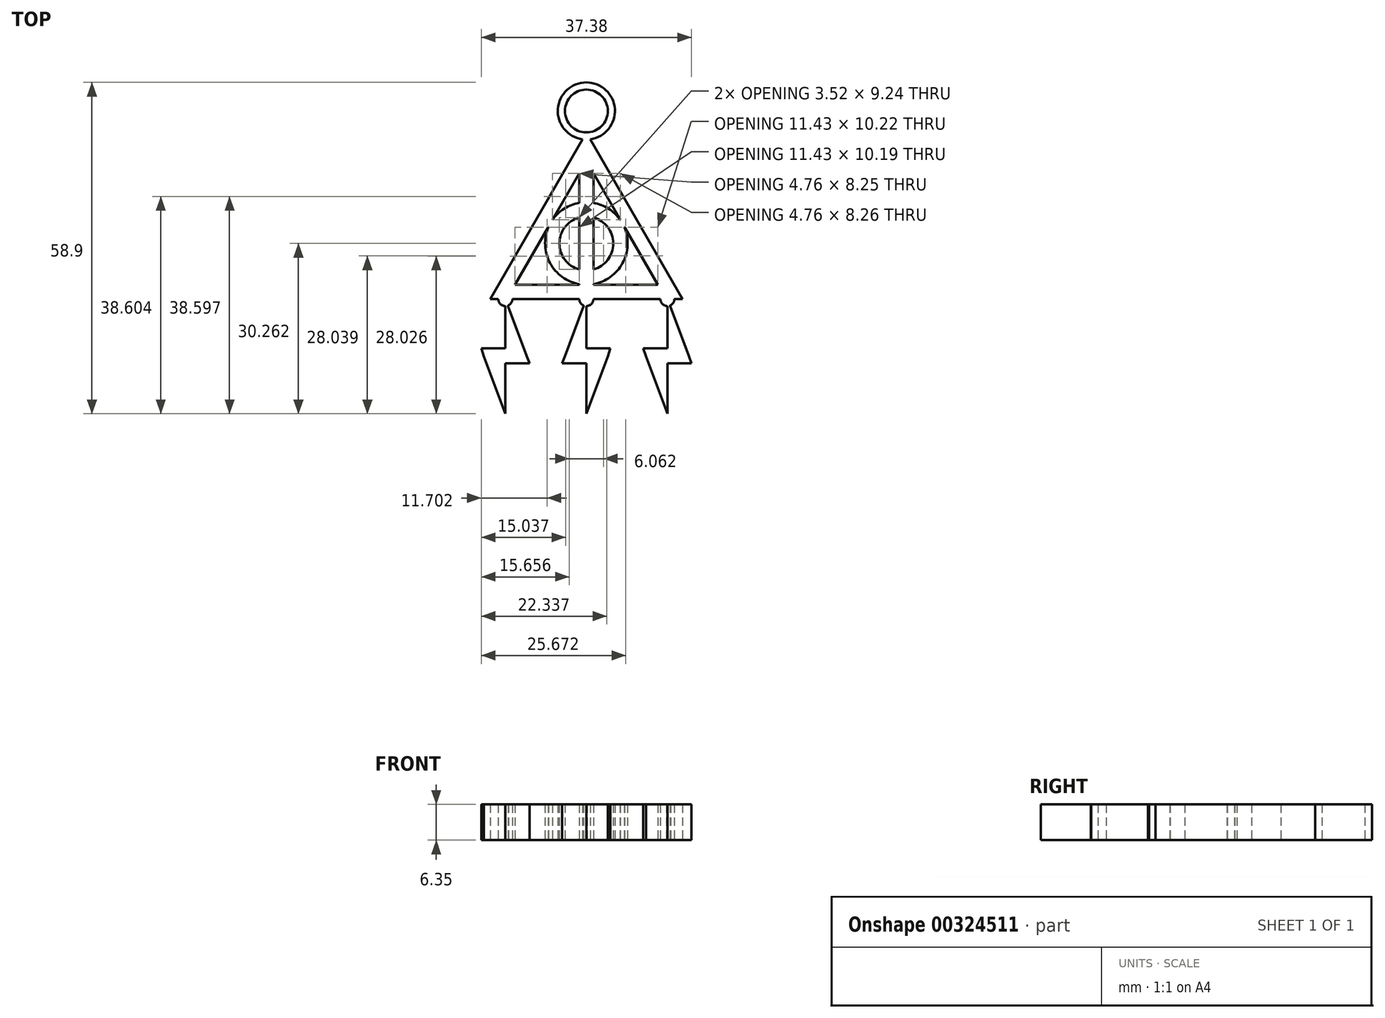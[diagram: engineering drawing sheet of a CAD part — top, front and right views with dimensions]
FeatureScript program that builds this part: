
annotation { "Feature Type Name" : "Feature", "Feature Type Description" : "" }
export const myFeature = defineFeature(function(context is Context, id is Id, definition is map)
    precondition{}
    {
        {
            var Q0;
            Q0=qCreatedBy(makeId("Top.planeOp"),FACE);
            var sketch = newSketch(context, id + "F0", { "sketchPlane" : qUnion([Q0])});
            skLineSegment(sketch, "E0", {"start": v(-43.23, 46.2) * mm, "end": v(-48, 37.96) * mm});
            skLineSegment(sketch, "E1", {"start": v(-54.66, 26.4) * mm, "end": v(-43.23, 26.4) * mm});
            skLineSegment(sketch, "E2", {"start": v(-40.7, 46.2) * mm, "end": v(-35.93, 37.96) * mm});
            skLineSegment(sketch, "E3.0", {"start": v(-42.67, 52.27) * mm, "end": v(-59.06, 23.87) * mm});
            skLineSegment(sketch, "E3.1", {"start": v(-41.26, 52.27) * mm, "end": v(-24.86, 23.87) * mm});
            skLineSegment(sketch, "E3.2", {"start": v(-59.06, 23.87) * mm, "end": v(-57.62, 23.87) * mm});
            skArc(sketch, "E4", {"start": v(-40.7, 26.52) * mm, "mid": v(-35.52, 30.24) * mm, "end": v(-35.21, 36.6) * mm});
            skArc(sketch, "E5.0", {"start": v(-40.7, 29.12) * mm, "mid": v(-37.17, 33.74) * mm, "end": v(-40.7, 38.36) * mm});
            skLineSegment(sketch, "E6.trimOffspring", {"start": v(-40.7, 26.4) * mm, "end": v(-29.26, 26.4) * mm});
            skArc(sketch, "E7.trimOffspring", {"start": v(-43.23, 38.36) * mm, "mid": v(-46.76, 33.74) * mm, "end": v(-43.23, 29.12) * mm});
            skArc(sketch, "E8.trimOffspring", {"start": v(-43.23, 40.96) * mm, "mid": v(-45.9, 39.93) * mm, "end": v(-47.96, 37.96) * mm});
            skLineSegment(sketch, "E9.trimOffspring", {"start": v(-40.7, 26.52) * mm, "end": v(-40.7, 26.4) * mm});
            skLineSegment(sketch, "E10.trimOffspring", {"start": v(-43.23, 26.52) * mm, "end": v(-43.23, 26.4) * mm});
            skLineSegment(sketch, "E11.trimOffspring", {"start": v(-43.23, 40.96) * mm, "end": v(-43.23, 46.2) * mm});
            skLineSegment(sketch, "E12.trimOffspring", {"start": v(-40.7, 40.96) * mm, "end": v(-40.7, 46.2) * mm});
            skLineSegment(sketch, "E13", {"start": v(-40.7, 29.12) * mm, "end": v(-40.7, 38.36) * mm});
            skLineSegment(sketch, "E14", {"start": v(-43.23, 29.12) * mm, "end": v(-43.23, 38.36) * mm});
            skLineSegment(sketch, "E15", {"start": v(-38.15, 13.64) * mm, "end": v(-41.96, 3.48) * mm});
            skLineSegment(sketch, "E16", {"start": v(-45.77, 13.7) * mm, "end": v(-42.44, 22.6) * mm});
            skLineSegment(sketch, "E17", {"start": v(-41.96, 22.46) * mm, "end": v(-41.96, 15.1) * mm});
            skLineSegment(sketch, "E18", {"start": v(-41.96, 12.4) * mm, "end": v(-41.96, 3.48) * mm});
            skLineSegment(sketch, "E19", {"start": v(-46.26, 12.44) * mm, "end": v(-45.77, 13.7) * mm});
            skLineSegment(sketch, "E20", {"start": v(-41.96, 12.4) * mm, "end": v(-46.26, 12.44) * mm});
            skLineSegment(sketch, "E21", {"start": v(-41.96, 15.1) * mm, "end": v(-37.67, 15.1) * mm});
            skLineSegment(sketch, "E22", {"start": v(-37.67, 15.1) * mm, "end": v(-38.15, 13.64) * mm});
            skArc(sketch, "E23", {"start": v(-43.22, 23.87) * mm, "mid": v(-43.02, 23.2) * mm, "end": v(-42.5, 22.73) * mm});
            skLineSegment(sketch, "E24.trimOffspring", {"start": v(-32.78, 23.87) * mm, "end": v(-28.82, 23.87) * mm});
            skArc(sketch, "E25.trimOffspring", {"start": v(-41.84, 22.62) * mm, "mid": v(-41.03, 23.02) * mm, "end": v(-40.7, 23.87) * mm});
            skLineSegment(sketch, "E26", {"start": v(-47.18, 23.87) * mm, "end": v(-43.22, 23.87) * mm});
            skLineSegment(sketch, "E27", {"start": v(-40.7, 23.87) * mm, "end": v(-36.74, 23.87) * mm});
            skLineSegment(sketch, "E28", {"start": v(-36.74, 23.87) * mm, "end": v(-32.78, 23.87) * mm});
            skLineSegment(sketch, "E29.MirrorCS", {"start": v(-47.18, 23.87) * mm, "end": v(-51.14, 23.87) * mm});
            skLineSegment(sketch, "E30.MirrorCS", {"start": v(-27.56, 22.43) * mm, "end": v(-27.56, 15.1) * mm});
            skLineSegment(sketch, "E31.MirrorCS", {"start": v(-23.75, 13.7) * mm, "end": v(-27.06, 22.53) * mm});
            skLineSegment(sketch, "E32.MirrorCS", {"start": v(-27.56, 12.4) * mm, "end": v(-23.27, 12.44) * mm});
            skLineSegment(sketch, "E33.MirrorCS", {"start": v(-27.56, 12.4) * mm, "end": v(-27.56, 3.48) * mm});
            skLineSegment(sketch, "E34.MirrorCS", {"start": v(-31.37, 13.64) * mm, "end": v(-27.56, 3.48) * mm});
            skLineSegment(sketch, "E35.MirrorCS", {"start": v(-27.56, 15.1) * mm, "end": v(-31.86, 15.1) * mm});
            skLineSegment(sketch, "E36.MirrorCS", {"start": v(-23.27, 12.44) * mm, "end": v(-23.75, 13.7) * mm});
            skLineSegment(sketch, "E37.MirrorCS", {"start": v(-31.86, 15.1) * mm, "end": v(-31.37, 13.64) * mm});
            skArc(sketch, "E38.MirrorCS", {"start": v(-27.73, 22.62) * mm, "mid": v(-28.5, 23.04) * mm, "end": v(-28.82, 23.87) * mm});
            skArc(sketch, "E39.MirrorCS", {"start": v(-26.3, 23.87) * mm, "mid": v(-26.5, 23.21) * mm, "end": v(-27, 22.75) * mm});
            skLineSegment(sketch, "E40.trimOffspring", {"start": v(-26.3, 23.87) * mm, "end": v(-24.86, 23.87) * mm});
            skLineSegment(sketch, "E41.MirrorCS", {"start": v(-52.55, 13.7) * mm, "end": v(-55.86, 22.53) * mm});
            skLineSegment(sketch, "E42.MirrorCS", {"start": v(-56.36, 22.49) * mm, "end": v(-56.36, 15.1) * mm});
            skLineSegment(sketch, "E43.MirrorCS", {"start": v(-56.36, 15.1) * mm, "end": v(-60.65, 15.1) * mm});
            skLineSegment(sketch, "E44.MirrorCS", {"start": v(-60.17, 13.64) * mm, "end": v(-56.36, 3.48) * mm});
            skLineSegment(sketch, "E45.MirrorCS", {"start": v(-56.36, 12.4) * mm, "end": v(-56.36, 3.48) * mm});
            skLineSegment(sketch, "E46.MirrorCS", {"start": v(-56.36, 12.4) * mm, "end": v(-52.06, 12.44) * mm});
            skLineSegment(sketch, "E47.MirrorCS", {"start": v(-52.06, 12.44) * mm, "end": v(-52.55, 13.7) * mm});
            skLineSegment(sketch, "E48.MirrorCS", {"start": v(-60.65, 15.1) * mm, "end": v(-60.17, 13.64) * mm});
            skArc(sketch, "E49.MirrorCS", {"start": v(-56.47, 22.62) * mm, "mid": v(-57.29, 23.02) * mm, "end": v(-57.62, 23.87) * mm});
            skArc(sketch, "E50.MirrorCS", {"start": v(-55.1, 23.87) * mm, "mid": v(-55.29, 23.21) * mm, "end": v(-55.8, 22.75) * mm});
            skLineSegment(sketch, "E51.trimOffspring", {"start": v(-55.1, 23.87) * mm, "end": v(-51.14, 23.87) * mm});
            skArc(sketch, "E52", {"start": v(-41.26, 52.27) * mm, "mid": v(-41.96, 62.38) * mm, "end": v(-42.67, 52.27) * mm});
            skCircle(sketch, "E53", {"center": v(-41.96, 57.3) * mm, "radius": 3.81 * mm});
            skArc(sketch, "E54.trimOffspring", {"start": v(-48.71, 36.6) * mm, "mid": v(-48.4, 30.24) * mm, "end": v(-43.23, 26.52) * mm});
            skLineSegment(sketch, "E55.trimOffspring", {"start": v(-48.78, 36.6) * mm, "end": v(-54.66, 26.4) * mm});
            skLineSegment(sketch, "E56", {"start": v(-35.96, 37.95) * mm, "end": v(-35.93, 37.96) * mm});
            skLineSegment(sketch, "E57", {"start": v(-35.16, 36.63) * mm, "end": v(-35.21, 36.6) * mm});
            skLineSegment(sketch, "E58.trimOffspring", {"start": v(-35.16, 36.63) * mm, "end": v(-29.26, 26.4) * mm});
            skArc(sketch, "E59.trimOffspring", {"start": v(-35.96, 37.95) * mm, "mid": v(-38.02, 39.93) * mm, "end": v(-40.7, 40.96) * mm});
            skLineSegment(sketch, "E60.trimOffspring", {"start": v(-48.71, 36.6) * mm, "end": v(-48.78, 36.6) * mm});
            skLineSegment(sketch, "E61.trimOffspring", {"start": v(-47.96, 37.96) * mm, "end": v(-48, 37.96) * mm});
            skArc(sketch, "E62", {"start": v(-55.8, 22.75) * mm, "mid": v(-55.86, 22.65) * mm, "end": v(-55.86, 22.53) * mm});
            skArc(sketch, "E63", {"start": v(-42.44, 22.6) * mm, "mid": v(-42.44, 22.68) * mm, "end": v(-42.5, 22.73) * mm});
            skArc(sketch, "E64", {"start": v(-27, 22.75) * mm, "mid": v(-27.07, 22.65) * mm, "end": v(-27.06, 22.53) * mm});
            skArc(sketch, "E65", {"start": v(-56.36, 22.49) * mm, "mid": v(-56.4, 22.57) * mm, "end": v(-56.47, 22.62) * mm});
            skArc(sketch, "E66", {"start": v(-41.84, 22.62) * mm, "mid": v(-41.93, 22.56) * mm, "end": v(-41.96, 22.46) * mm});
            skArc(sketch, "E67", {"start": v(-27.56, 22.43) * mm, "mid": v(-27.6, 22.55) * mm, "end": v(-27.73, 22.62) * mm});
            skSolve(sketch);
        }
        {
            var Q0;
            {var subQ10=sQuery(id+"F0.wireOp",EDGE,"E1");Q0=makeQuery(id+"F0.imprint","IMPRINT",FACE,{"disambiguationData":[TD([[makeQuery(id+"F0.imprint","IMPRINT",EDGE,{"derivedFrom":subQ10}),-1.0]])]});}
            extrude(context, id + "F1", {"entities" : qUnion([Q0]), "depth" : 6.35 * mm});
        }
    });
